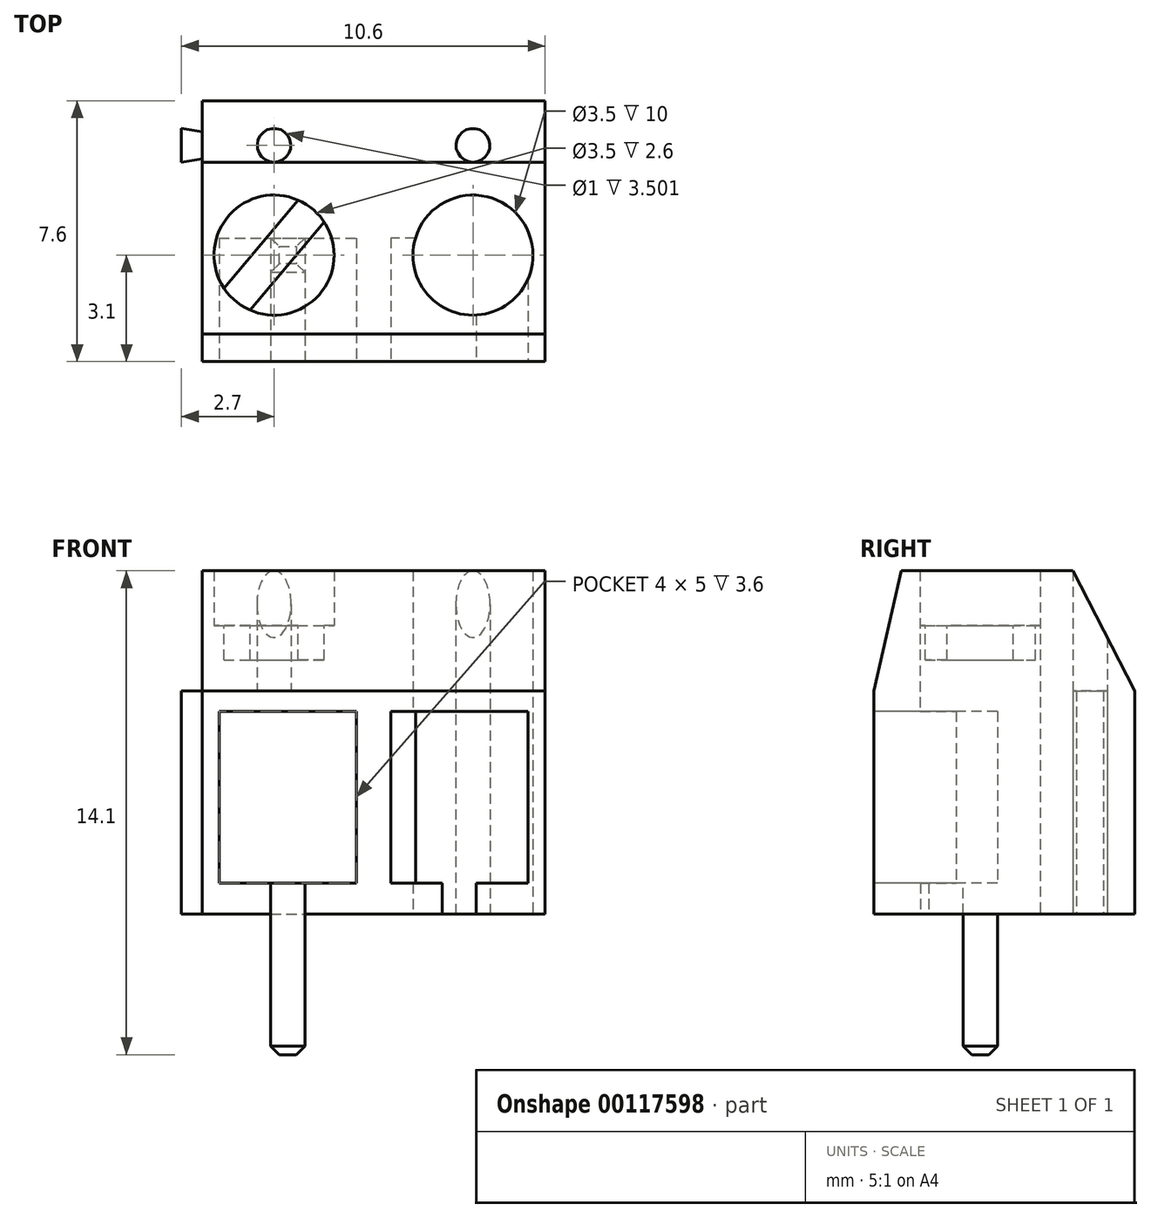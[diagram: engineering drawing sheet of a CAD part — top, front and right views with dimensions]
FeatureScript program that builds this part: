
annotation { "Feature Type Name" : "Feature", "Feature Type Description" : "" }
export const myFeature = defineFeature(function(context is Context, id is Id, definition is map)
    precondition{}
    {
        {
            var Q0;
            Q0=qCreatedBy(makeId("Top.planeOp"),FACE);
            var sketch = newSketch(context, id + "F0", { "sketchPlane" : qUnion([Q0])});
            skLineSegment(sketch, "E0.bottom", {"start": v(-5, 3.8) * mm, "end": v(5, 3.8) * mm});
            skLineSegment(sketch, "E0.top", {"start": v(-5, -3.8) * mm, "end": v(5, -3.8) * mm});
            skLineSegment(sketch, "E0.left", {"start": v(-5, 3.8) * mm, "end": v(-5, -3.8) * mm});
            skLineSegment(sketch, "E0.right", {"start": v(5, 3.8) * mm, "end": v(5, -3.8) * mm});
            skLineSegment(sketch, "E1", {"start": v(0, 3.8) * mm, "end": v(0, -3.8) * mm, "construction": true});
            skLineSegment(sketch, "E2", {"start": v(5, -0.7) * mm, "end": v(-5, -0.7) * mm, "construction": true});
            skLineSegment(sketch, "E3", {"start": v(2.9, 3.8) * mm, "end": v(2.9, -3.8) * mm, "construction": true});
            skLineSegment(sketch, "E4", {"start": v(-2.9, 3.8) * mm, "end": v(-2.9, -3.8) * mm, "construction": true});
            skCircle(sketch, "E5", {"center": v(-2.9, -0.7) * mm, "radius": 1.75 * mm});
            skCircle(sketch, "E6.MirrorC", {"center": v(2.9, -0.7) * mm, "radius": 1.75 * mm});
            skLineSegment(sketch, "E7.bottom", {"start": v(-5, 2.9) * mm, "end": v(-5.6, 3) * mm});
            skLineSegment(sketch, "E7.top", {"start": v(-5, 2.1) * mm, "end": v(-5.6, 2) * mm});
            skLineSegment(sketch, "E7.left", {"start": v(-5, 2.9) * mm, "end": v(-5, 2.1) * mm});
            skLineSegment(sketch, "E7.right", {"start": v(-5.6, 3) * mm, "end": v(-5.6, 2) * mm});
            skLineSegment(sketch, "E8", {"start": v(-5, 2) * mm, "end": v(5, 2) * mm});
            skCircle(sketch, "E9", {"center": v(-2.9, 2.5) * mm, "radius": 0.5 * mm});
            skCircle(sketch, "E10.MirrorC", {"center": v(2.9, 2.5) * mm, "radius": 0.5 * mm});
            skLineSegment(sketch, "E11", {"start": v(-5, -3) * mm, "end": v(5, -3) * mm});
            skSolve(sketch);
        }
        {
            var Q0;
            {var subQ1=sQuery(id+"F0.wireOp",EDGE,"E0.bottom");Q0=makeQuery(id+"F0.imprint","IMPRINT",FACE,{"disambiguationData":[TD([[makeQuery(id+"F0.imprint","IMPRINT",EDGE,{"derivedFrom":subQ1}),-1.0]])]});}
            var Q1;
            Q1=makeQuery(id+"F0.imprint","IMPRINT",FACE,{"disambiguationData":[TD([[makeQuery(id+"F0.imprint","IMPRINT",EDGE,{"derivedFrom":sQuery(id+"F0.wireOp",EDGE,"E5")}),-1.0]])]});
            var Q2;
            {var subQ0=sQuery(id+"F0.wireOp",EDGE,"E0.top");Q2=makeQuery(id+"F0.imprint","IMPRINT",FACE,{"disambiguationData":[TD([[makeQuery(id+"F0.imprint","IMPRINT",EDGE,{"derivedFrom":subQ0}),1.0]])]});}
            var Q3;
            Q3=makeQuery(id+"F0.imprint","IMPRINT",FACE,{"disambiguationData":[TD([[makeQuery(id+"F0.imprint","IMPRINT",EDGE,{"derivedFrom":sQuery(id+"F0.wireOp",EDGE,"E6.MirrorC")}),-1.0]])]});
            var Q4;
            Q4=makeQuery(id+"F0.imprint","IMPRINT",FACE,{"disambiguationData":[TD([[makeQuery(id+"F0.imprint","IMPRINT",EDGE,{"derivedFrom":sQuery(id+"F0.wireOp",EDGE,"E5")}),1.0]])]});
            var Q5;
            Q5=makeQuery(id+"F0.imprint","IMPRINT",FACE,{"disambiguationData":[TD([[makeQuery(id+"F0.imprint","IMPRINT",EDGE,{"derivedFrom":sQuery(id+"F0.wireOp",EDGE,"E7.bottom")}),1.0]])]});
            var Q6;
            Q6=makeQuery(id+"F0.imprint","IMPRINT",FACE,{"disambiguationData":[TD([[makeQuery(id+"F0.imprint","IMPRINT",EDGE,{"derivedFrom":sQuery(id+"F0.wireOp",EDGE,"E9")}),1.0]])]});
            var Q7;
            Q7=makeQuery(id+"F0.imprint","IMPRINT",FACE,{"disambiguationData":[TD([[makeQuery(id+"F0.imprint","IMPRINT",EDGE,{"derivedFrom":sQuery(id+"F0.wireOp",EDGE,"E10.MirrorC")}),-1.0]])]});
            extrude(context, id + "F1", {"entities" : qUnion([Q0, Q1, Q2, Q3, Q4, Q5, Q6, Q7]), "depth" : 6.5 * mm});
        }
        {
            var Q0;
            Q0=makeQuery(id+"F0.imprint","IMPRINT",FACE,{"disambiguationData":[TD([[makeQuery(id+"F0.imprint","IMPRINT",EDGE,{"derivedFrom":sQuery(id+"F0.wireOp",EDGE,"E6.MirrorC")}),-1.0]])]});
            var Q1;
            Q1=makeQuery(id+"F0.imprint","IMPRINT",FACE,{"disambiguationData":[TD([[makeQuery(id+"F0.imprint","IMPRINT",EDGE,{"derivedFrom":sQuery(id+"F0.wireOp",EDGE,"E5")}),1.0]])]});
            extrude(context, id + "F2", {"entities" : qUnion([Q0, Q1]), "operationType" : NewBodyOperationType.ADD, "depth" : 8.4 * mm});
        }
        {
            var Q0;
            Q0=makeQuery(id+"F0.imprint","IMPRINT",FACE,{"disambiguationData":[TD([[makeQuery(id+"F0.imprint","IMPRINT",EDGE,{"derivedFrom":sQuery(id+"F0.wireOp",EDGE,"E5")}),-1.0]])]});
            extrude(context, id + "F3", {"entities" : qUnion([Q0]), "operationType" : NewBodyOperationType.ADD, "depth" : 10 * mm});
        }
        {
            var Q0;
            {var subQ0=sQuery(id+"F0.wireOp",EDGE,"E0.right");Q0=makeQuery(id+"F3.boolean.opBoolean","MERGE",FACE,{"derivedFrom":[makeQuery(id+"F1.opExtrude","SWEPT_FACE",FACE,{"disambiguationData":[OSD([subQ0])]}),makeQuery(id+"F3.opExtrude","SWEPT_FACE",FACE,{"disambiguationData":[OSD([subQ0])]})]});}
            var sketch = newSketch(context, id + "F4", { "sketchPlane" : qUnion([Q0])});
            skLineSegment(sketch, "E12.0", {"start": v(-3, 10) * mm, "end": v(-3, 6.5) * mm});
            skLineSegment(sketch, "E13.0", {"start": v(-3, 6.5) * mm, "end": v(-3.8, 6.5) * mm});
            skLineSegment(sketch, "E14.0", {"start": v(3.8, 6.5) * mm, "end": v(2, 6.5) * mm});
            skLineSegment(sketch, "E15.0", {"start": v(2, 10) * mm, "end": v(2, 6.5) * mm});
            skLineSegment(sketch, "E16", {"start": v(-3, 10) * mm, "end": v(-3.8, 6.5) * mm});
            skLineSegment(sketch, "E17", {"start": v(2, 10) * mm, "end": v(3.8, 6.5) * mm});
            skSolve(sketch);
        }
        {
            var Q0;
            Q0=makeQuery(id+"F4.imprint","IMPRINT",FACE,{"disambiguationData":[TD([[makeQuery(id+"F4.imprint","IMPRINT",EDGE,{"derivedFrom":sQuery(id+"F4.wireOp",EDGE,"E12.0")}),-1.0]])]});
            var Q1;
            Q1=makeQuery(id+"F4.imprint","IMPRINT",FACE,{"disambiguationData":[TD([[makeQuery(id+"F4.imprint","IMPRINT",EDGE,{"derivedFrom":sQuery(id+"F4.wireOp",EDGE,"E14.0")}),-1.0]])]});
            var Q2;
            {var subQ0=sQuery(id+"F0.wireOp",EDGE,"E0.left");var subQ2=makeQuery(id+"F0.imprint","INTERSECT",VERTEX,{"derivedFrom":[subQ0,sQuery(id+"F0.wireOp",EDGE,"E8")]});Q2=makeQuery(id+"F3.boolean.opBoolean","MERGE",FACE,{"derivedFrom":[makeQuery(id+"F1.opExtrude","SWEPT_FACE",FACE,{"disambiguationData":[OSD([subQ0]),TDD([makeQuery(id+"F0.imprint","IMPRINT",EDGE,{"disambiguationData":[TD([[subQ2,1.0]])],"derivedFrom":subQ0}),makeQuery(id+"F0.imprint","IMPRINT",EDGE,{"disambiguationData":[TD([[subQ2,-1.0]])],"derivedFrom":subQ0}),makeQuery(id+"F0.imprint","IMPRINT",EDGE,{"disambiguationData":[TD([[makeQuery(id+"F0.imprint","INTERSECT",VERTEX,{"derivedFrom":[sQuery(id+"F0.wireOp",EDGE,"E0.top"),subQ0]}),1.0]])],"derivedFrom":subQ0})])]}),makeQuery(id+"F3.opExtrude","SWEPT_FACE",FACE,{"disambiguationData":[OSD([subQ0])]})]});}
            extrude(context, id + "F5", {"entities" : qUnion([Q0, Q1]), "operationType" : NewBodyOperationType.ADD, "endBound" : BoundingType.UP_TO_SURFACE, "oppositeDirection" : true, "endBoundEntityFace" : qUnion([Q2]), "depth" : 25 * mm});
        }
        {
            var Q0;
            {var subQ0=sQuery(id+"F0.wireOp",EDGE,"E0.right");var subQ1=sQuery(id+"F0.wireOp",EDGE,"E0.left");var subQ2=sQuery(id+"F0.wireOp",EDGE,"E0.top");var subQ7=sQuery(id+"F0.wireOp",EDGE,"E7.top");var subQ8=sQuery(id+"F0.wireOp",EDGE,"E0.bottom");var subQ9=sQuery(id+"F0.wireOp",EDGE,"E7.bottom");var subQ10=sQuery(id+"F0.wireOp",EDGE,"E7.right");Q0=makeQuery(id+"F3.boolean.opBoolean","SPLIT",FACE,{"disambiguationData":[TD([makeQuery(id+"F1.opExtrude","SWEPT_FACE",FACE,{"disambiguationData":[OSD([subQ8])]})])],"derivedFrom":makeQuery(id+"F1.opExtrude","CAP_FACE",FACE,{"disambiguationData":[OSD([subQ8,subQ2,subQ1,subQ0,subQ9,subQ7,subQ10])],"isStart":false})});}
            var sketch = newSketch(context, id + "F6", { "sketchPlane" : qUnion([Q0])});
            skCircle(sketch, "E18.0", {"center": v(-2.9, 2.5) * mm, "radius": 0.5 * mm});
            skCircle(sketch, "E19.0", {"center": v(2.9, 2.5) * mm, "radius": 0.5 * mm});
            skSolve(sketch);
        }
        {
            var Q0;
            Q0 = qSketchRegion(id + "F6", true);
            extrude(context, id + "F7", {"entities" : qUnion([Q0]), "operationType" : NewBodyOperationType.REMOVE, "endBound" : BoundingType.THROUGH_ALL, "depth" : 25 * mm});
        }
        {
            var Q0;
            Q0=makeQuery(id+"F2.opExtrude","CAP_FACE",FACE,{"disambiguationData":[OSD([sQuery(id+"F0.wireOp",EDGE,"E6.MirrorC")])],"isStart":false});
            var sketch = newSketch(context, id + "F8", { "sketchPlane" : qUnion([Q0])});
            skCircle(sketch, "E20.0", {"center": v(-2.9, -0.7) * mm, "radius": 1.75 * mm});
            skCircle(sketch, "E21.0", {"center": v(2.9, -0.7) * mm, "radius": 1.75 * mm});
            skLineSegment(sketch, "E22", {"start": v(-4.36, -1.66) * mm, "end": v(-2.2, 0.9) * mm});
            skLineSegment(sketch, "E23", {"start": v(-3.6, -2.3) * mm, "end": v(-1.44, 0.26) * mm});
            skLineSegment(sketch, "E24", {"start": v(4.3, -1.74) * mm, "end": v(1.15, -0.6) * mm});
            skLineSegment(sketch, "E25", {"start": v(1.5, 0.34) * mm, "end": v(4.65, -0.8) * mm});
            skLineSegment(sketch, "E26", {"start": v(-3.28, -0.38) * mm, "end": v(-2.52, -1.02) * mm, "construction": true});
            skLineSegment(sketch, "E27", {"start": v(2.73, -1.17) * mm, "end": v(3.07, -0.23) * mm, "construction": true});
            skSolve(sketch);
        }
        {
            var Q0;
            {var subQ0=sQuery(id+"F8.wireOp",EDGE,"E22");Q0=makeQuery(id+"F8.imprint","IMPRINT",FACE,{"disambiguationData":[TD([[makeQuery(id+"F8.imprint","IMPRINT",EDGE,{"derivedFrom":subQ0}),-1.0]])]});}
            var Q1;
            {var subQ0=sQuery(id+"F8.wireOp",EDGE,"E24");Q1=makeQuery(id+"F8.imprint","IMPRINT",FACE,{"disambiguationData":[TD([[makeQuery(id+"F8.imprint","IMPRINT",EDGE,{"derivedFrom":subQ0}),-1.0]])]});}
            extrude(context, id + "F9", {"entities" : qUnion([Q0, Q1]), "operationType" : NewBodyOperationType.REMOVE, "oppositeDirection" : true, "depth" : 1 * mm});
        }
        {
            var Q0;
            Q0=makeQuery(id+"F1.opExtrude","SWEPT_FACE",FACE,{"disambiguationData":[OSD([sQuery(id+"F0.wireOp",EDGE,"E0.top")])]});
            var sketch = newSketch(context, id + "F10", { "sketchPlane" : qUnion([Q0])});
            skLineSegment(sketch, "E28", {"start": v(0, 0) * mm, "end": v(0, 6.5) * mm, "construction": true});
            skLineSegment(sketch, "E29.bottom", {"start": v(-4.5, 5.9) * mm, "end": v(-0.5, 5.9) * mm});
            skLineSegment(sketch, "E29.top", {"start": v(-4.5, 0.9) * mm, "end": v(-3, 0.9) * mm});
            skLineSegment(sketch, "E29.left", {"start": v(-4.5, 5.9) * mm, "end": v(-4.5, 0.9) * mm});
            skLineSegment(sketch, "E29.right", {"start": v(-0.5, 5.9) * mm, "end": v(-0.5, 0.9) * mm});
            skLineSegment(sketch, "E30", {"start": v(-2.5, 5.9) * mm, "end": v(-2.5, 0) * mm, "construction": true});
            skLineSegment(sketch, "E31", {"start": v(-3, 0.9) * mm, "end": v(-3, 0) * mm});
            skLineSegment(sketch, "E32.MirrorCS", {"start": v(-2, 0.9) * mm, "end": v(-2, 0) * mm});
            skLineSegment(sketch, "E33.trimOffspring", {"start": v(-2, 0.9) * mm, "end": v(-0.5, 0.9) * mm});
            skLineSegment(sketch, "E34.MirrorCS", {"start": v(0.5, 5.9) * mm, "end": v(0.5, 0.9) * mm});
            skLineSegment(sketch, "E35.MirrorCS", {"start": v(2, 0.9) * mm, "end": v(0.5, 0.9) * mm});
            skLineSegment(sketch, "E36.MirrorCS", {"start": v(2, 0.9) * mm, "end": v(2, 0) * mm});
            skLineSegment(sketch, "E37.MirrorCS", {"start": v(3, 0.9) * mm, "end": v(3, 0) * mm});
            skLineSegment(sketch, "E38.MirrorCS", {"start": v(4.5, 0.9) * mm, "end": v(3, 0.9) * mm});
            skLineSegment(sketch, "E39.MirrorCS", {"start": v(4.5, 5.9) * mm, "end": v(4.5, 0.9) * mm});
            skLineSegment(sketch, "E40.MirrorCS", {"start": v(4.5, 5.9) * mm, "end": v(0.5, 5.9) * mm});
            skSolve(sketch);
        }
        {
            var Q0;
            Q0=makeQuery(id+"F10.imprint","IMPRINT",FACE,{"disambiguationData":[TD([[makeQuery(id+"F10.imprint","IMPRINT",EDGE,{"derivedFrom":sQuery(id+"F10.wireOp",EDGE,"E29.bottom")}),-1.0]])]});
            var Q1;
            Q1=makeQuery(id+"F10.imprint","IMPRINT",FACE,{"disambiguationData":[TD([[makeQuery(id+"F10.imprint","IMPRINT",EDGE,{"derivedFrom":sQuery(id+"F10.wireOp",EDGE,"E34.MirrorCS")}),1.0]])]});
            extrude(context, id + "F11", {"entities" : qUnion([Q0, Q1]), "operationType" : NewBodyOperationType.REMOVE, "oppositeDirection" : true, "depth" : 3.6 * mm});
        }
        {
            var Q0;
            Q0=makeQuery(id+"F11.boolean.opBoolean","COPY",FACE,{"derivedFrom":makeQuery(id+"F11.opExtrude","SWEPT_FACE",FACE,{"disambiguationData":[OSD([sQuery(id+"F10.wireOp",EDGE,"E29.top")])]})});
            var sketch = newSketch(context, id + "F12", { "sketchPlane" : qUnion([Q0])});
            skLineSegment(sketch, "E41.0", {"start": v(-3, -0.2) * mm, "end": v(-2, -0.2) * mm});
            skLineSegment(sketch, "E41.1", {"start": v(2, -0.2) * mm, "end": v(3, -0.2) * mm});
            skLineSegment(sketch, "E42", {"start": v(-3, -0.2) * mm, "end": v(-3, -1.2) * mm});
            skLineSegment(sketch, "E43", {"start": v(-3, -1.2) * mm, "end": v(-2, -1.2) * mm});
            skLineSegment(sketch, "E44", {"start": v(-2, -1.2) * mm, "end": v(-2, -0.2) * mm});
            skLineSegment(sketch, "E45.MirrorCS", {"start": v(3, -0.2) * mm, "end": v(2, -0.2) * mm});
            skLineSegment(sketch, "E46.MirrorCS", {"start": v(3, -0.2) * mm, "end": v(3, -1.2) * mm});
            skLineSegment(sketch, "E47.MirrorCS", {"start": v(2, -1.2) * mm, "end": v(2, -0.2) * mm});
            skLineSegment(sketch, "E48.MirrorCS", {"start": v(3, -1.2) * mm, "end": v(2, -1.2) * mm});
            skSolve(sketch);
        }
        {
            var Q0;
            Q0=makeQuery(id+"F12.imprint","IMPRINT",FACE,{"disambiguationData":[TD([[makeQuery(id+"F12.imprint","IMPRINT",EDGE,{"derivedFrom":sQuery(id+"F12.wireOp",EDGE,"E41.0")}),-1.0]])]});
            var Q1;
            Q1=makeQuery(id+"F12.imprint","IMPRINT",FACE,{"disambiguationData":[TD([[makeQuery(id+"F12.imprint","IMPRINT",EDGE,{"derivedFrom":sQuery(id+"F12.wireOp",EDGE,"E45.MirrorCS")}),1.0]])]});
            extrude(context, id + "F13", {"entities" : qUnion([Q0, Q1]), "operationType" : NewBodyOperationType.ADD, "oppositeDirection" : true, "depth" : 5 * mm});
        }
        {
            var Q0;
            Q0=makeQuery(id+"F13.opExtrude","CAP_FACE",FACE,{"disambiguationData":[OSD([sQuery(id+"F12.wireOp",EDGE,"E41.0"),sQuery(id+"F12.wireOp",EDGE,"E42"),sQuery(id+"F12.wireOp",EDGE,"E43"),sQuery(id+"F12.wireOp",EDGE,"E44")])],"isStart":false});
            var Q1;
            Q1=makeQuery(id+"F13.opExtrude","CAP_FACE",FACE,{"disambiguationData":[OSD([sQuery(id+"F12.wireOp",EDGE,"E45.MirrorCS"),sQuery(id+"F12.wireOp",EDGE,"E46.MirrorCS"),sQuery(id+"F12.wireOp",EDGE,"E47.MirrorCS"),sQuery(id+"F12.wireOp",EDGE,"E48.MirrorCS")])],"isStart":false});
            chamfer(context, id + "F14", {"entities" : qUnion([Q0, Q1]), "width" : 0.25 * mm, "tangentPropagation" : true});
        }
    });
